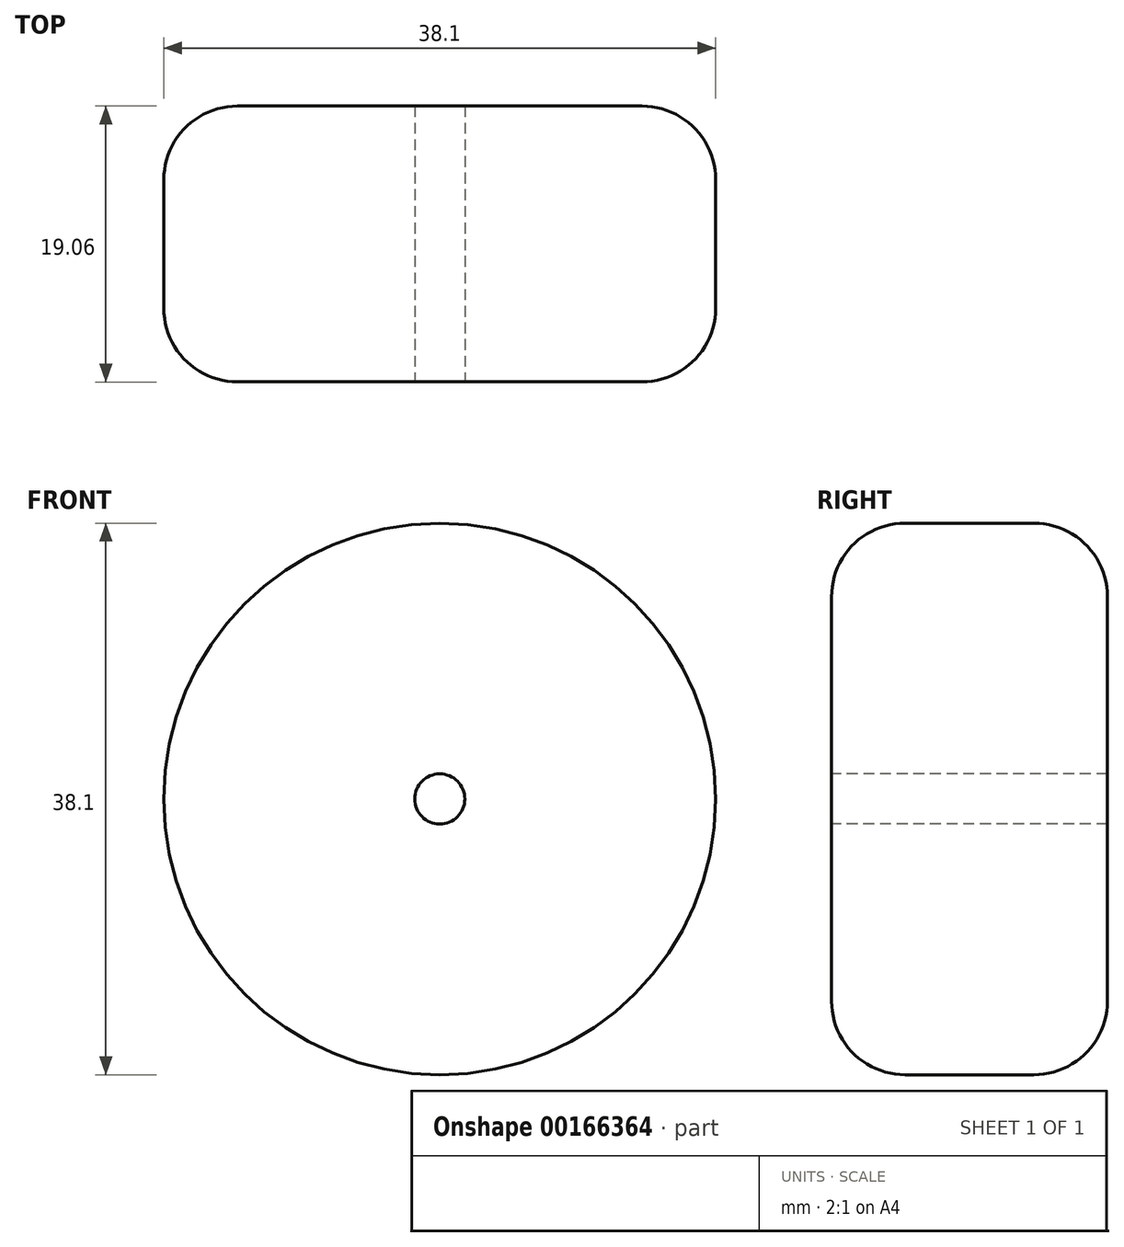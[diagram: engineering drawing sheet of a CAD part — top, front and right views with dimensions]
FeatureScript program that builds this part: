
annotation { "Feature Type Name" : "Feature", "Feature Type Description" : "" }
export const myFeature = defineFeature(function(context is Context, id is Id, definition is map)
    precondition{}
    {
        {
            var Q0;
            Q0=qCreatedBy(makeId("Front.planeOp"),FACE);
            var sketch = newSketch(context, id + "F0", { "sketchPlane" : qUnion([Q0])});
            skCircle(sketch, "E0", {"center": v(0, 0) * mm, "radius": 19.05 * mm});
            skSolve(sketch);
        }
        {
            var Q0;
            Q0=makeQuery(id+"F0.imprint","IMPRINT",FACE,{"disambiguationData":[TD([[makeQuery(id+"F0.imprint","IMPRINT",EDGE,{"derivedFrom":sQuery(id+"F0.wireOp",EDGE,"E0")}),1.0]])]});
            extrude(context, id + "F1", {"entities" : qUnion([Q0]), "endBound" : BoundingType.SYMMETRIC, "depth" : 19.05 * mm});
        }
        {
            var Q0;
            Q0=makeQuery(id+"F1.opExtrude","CAP_EDGE",EDGE,{"disambiguationData":[OSD([sQuery(id+"F0.wireOp",EDGE,"E0")])],"isStart":false});
            var Q1;
            Q1=makeQuery(id+"F1.opExtrude","CAP_EDGE",EDGE,{"disambiguationData":[OSD([sQuery(id+"F0.wireOp",EDGE,"E0")])],"isStart":true});
            fillet(context, id + "F2", {"entities" : qUnion([Q0, Q1]), "radius" : 5.08 * mm, "tangentPropagation" : true, "allowEdgeOverflow" : false});
        }
        {
            var Q0;
            Q0=makeQuery(id+"F1.opExtrude","CAP_FACE",FACE,{"disambiguationData":[OSD([sQuery(id+"F0.wireOp",EDGE,"E0")])],"isStart":false});
            var sketch = newSketch(context, id + "F3", { "sketchPlane" : qUnion([Q0])});
            skCircle(sketch, "E1", {"center": v(0, 0) * mm, "radius": 1.73 * mm});
            skSolve(sketch);
        }
        {
            var Q0;
            Q0=makeQuery(id+"F3.imprint","IMPRINT",FACE,{"disambiguationData":[TD([[makeQuery(id+"F3.imprint","IMPRINT",EDGE,{"derivedFrom":sQuery(id+"F3.wireOp",EDGE,"E1")}),1.0]])]});
            extrude(context, id + "F4", {"entities" : qUnion([Q0]), "operationType" : NewBodyOperationType.REMOVE, "oppositeDirection" : true, "depth" : 19.05 * mm});
        }
    });
